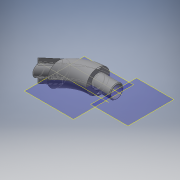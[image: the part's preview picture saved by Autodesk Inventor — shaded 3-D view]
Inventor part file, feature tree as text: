
AUTODESK INVENTOR PART (.ipt)
format: ipt  version: 2016 (Build 200138000, 138)  size: 307,712 bytes
history: native  units: mm
features: sketch x13, sweep x5, other x4, fillet x4, extrude x3
ambient origin geometry x8: Origin, YZ Plane, XZ Plane, XY Plane, X Axis, Y Axis, Z Axis, Center Point
bodies: Solide1 (feature_tree)
feature tree (29):
  sweep  "Balayage1"
  extrude  "Extrusion1"  Depth=27.0mm
  other  "Plan de construction1"
  sketch  "Esquisse4"
  sweep  "Balayage2"
  fillet  "Congé1"  Radius=16.0mm
  extrude  "Extrusion3"  Depth=14.0mm
  other  "Plan de construction2"
  sweep  "Balayage3"
  sweep  "Balayage4"
  sweep  "Balayage5"
  fillet  "Congé2"  Radius=2.0mm
  fillet  "Congé3"  Radius=35.0mm
  fillet  "Congé4"  Radius=20.0mm
  extrude  "Extrusion4"  TaperAngle=0.0deg  [1 undecoded]
  sketch  "Esquisse1"
  sketch  "Esquisse2"
  sketch  "Esquisse3"
  other  "Axe de construction1"
  other  "Axe de construction2"
  sketch  "Esquisse6"
  sketch  "Esquisse8"
  sketch  "Esquisse10"
  sketch  "Esquisse11"
  sketch  "Esquisse12"
  sketch  "Esquisse13"
  sketch  "Esquisse14"
  sketch  "Esquisse15"
  sketch  "Esquisse16"
note: 1 required parameter value undecoded (feature->parameter linkage not recoverable at this tier; creation-order binding heuristic only, values carry confidence <= 0.55)
